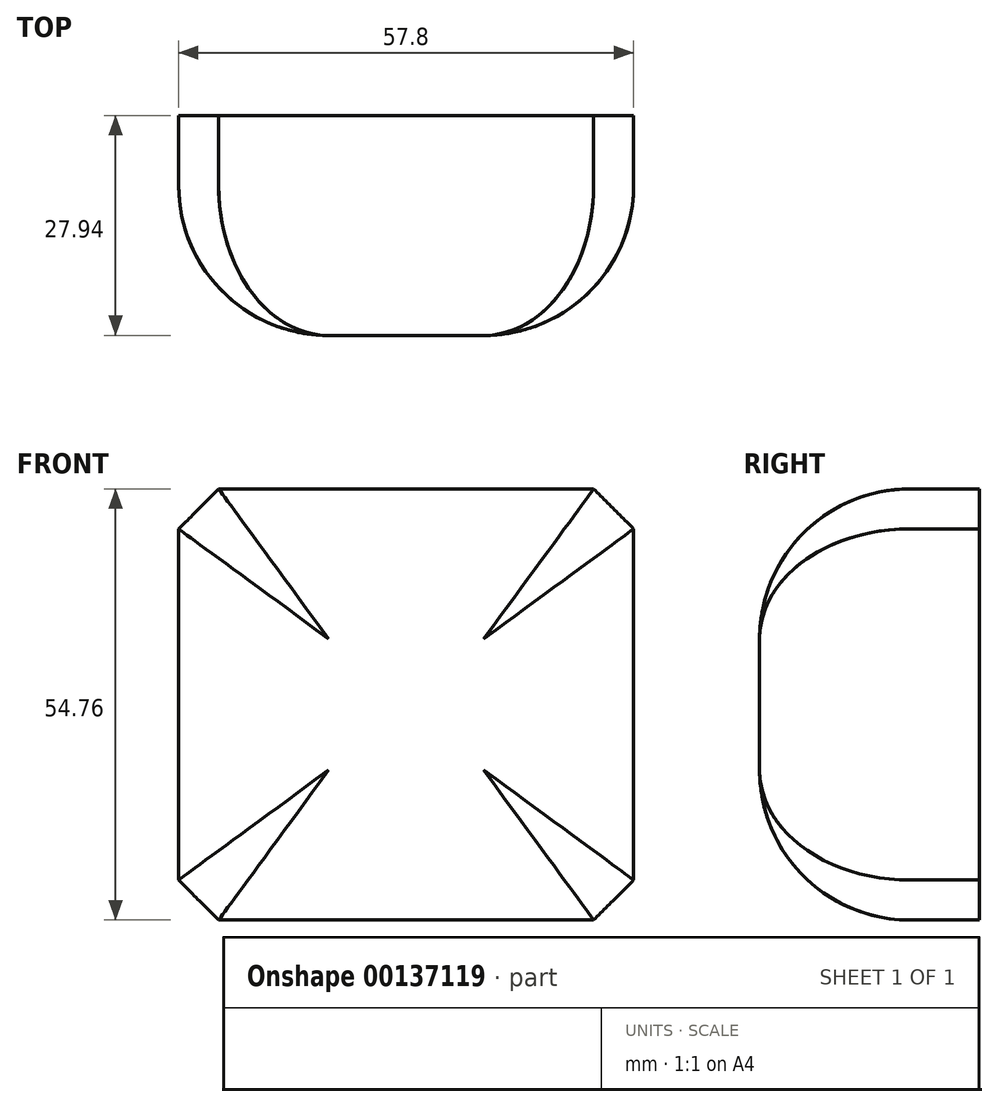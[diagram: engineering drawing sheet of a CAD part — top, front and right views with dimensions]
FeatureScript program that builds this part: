
annotation { "Feature Type Name" : "Feature", "Feature Type Description" : "" }
export const myFeature = defineFeature(function(context is Context, id is Id, definition is map)
    precondition{}
    {
        {
            var Q0;
            Q0=qCreatedBy(makeId("Front.planeOp"),FACE);
            var sketch = newSketch(context, id + "F0", { "sketchPlane" : qUnion([Q0])});
            skLineSegment(sketch, "E0.bottom", {"start": v(-40.16, 61.96) * mm, "end": v(17.64, 61.96) * mm});
            skLineSegment(sketch, "E0.top", {"start": v(-40.16, 7.2) * mm, "end": v(17.64, 7.2) * mm});
            skLineSegment(sketch, "E0.left", {"start": v(-40.16, 61.96) * mm, "end": v(-40.16, 7.2) * mm});
            skLineSegment(sketch, "E0.right", {"start": v(17.64, 61.96) * mm, "end": v(17.64, 7.2) * mm});
            skSolve(sketch);
        }
        {
            var Q0;
            Q0=makeQuery(id+"F0.imprint","IMPRINT",FACE,{"disambiguationData":[TD([[makeQuery(id+"F0.imprint","IMPRINT",EDGE,{"derivedFrom":sQuery(id+"F0.wireOp",EDGE,"E0.bottom")}),-1.0]])]});
            extrude(context, id + "F1", {"entities" : qUnion([Q0]), "depth" : 27.94 * mm});
        }
        {
            var Q0;
            Q0=makeQuery(id+"F1.opExtrude","CAP_EDGE",EDGE,{"disambiguationData":[OSD([sQuery(id+"F0.wireOp",EDGE,"E0.bottom")])],"isStart":false});
            var Q1;
            Q1=makeQuery(id+"F1.opExtrude","CAP_EDGE",EDGE,{"disambiguationData":[OSD([sQuery(id+"F0.wireOp",EDGE,"E0.right")])],"isStart":false});
            var Q2;
            Q2=makeQuery(id+"F1.opExtrude","CAP_EDGE",EDGE,{"disambiguationData":[OSD([sQuery(id+"F0.wireOp",EDGE,"E0.top")])],"isStart":false});
            var Q3;
            Q3=makeQuery(id+"F1.opExtrude","CAP_EDGE",EDGE,{"disambiguationData":[OSD([sQuery(id+"F0.wireOp",EDGE,"E0.left")])],"isStart":false});
            fillet(context, id + "F2", {"entities" : qUnion([Q0, Q1, Q2, Q3]), "radius" : 19.05 * mm, "tangentPropagation" : true, "allowEdgeOverflow" : false});
        }
        {
            var Q0;
            Q0=makeQuery(id+"F1.opExtrude","SWEPT_EDGE",EDGE,{"disambiguationData":[OSD([sQuery(id+"F0.wireOp",EDGE,"E0.bottom"),sQuery(id+"F0.wireOp",EDGE,"E0.right")])]});
            var Q1;
            Q1=makeQuery(id+"F1.opExtrude","SWEPT_EDGE",EDGE,{"disambiguationData":[OSD([sQuery(id+"F0.wireOp",EDGE,"E0.top"),sQuery(id+"F0.wireOp",EDGE,"E0.right")])]});
            var Q2;
            Q2=makeQuery(id+"F1.opExtrude","SWEPT_EDGE",EDGE,{"disambiguationData":[OSD([sQuery(id+"F0.wireOp",EDGE,"E0.bottom"),sQuery(id+"F0.wireOp",EDGE,"E0.left")])]});
            var Q3;
            Q3=makeQuery(id+"F1.opExtrude","SWEPT_EDGE",EDGE,{"disambiguationData":[OSD([sQuery(id+"F0.wireOp",EDGE,"E0.top"),sQuery(id+"F0.wireOp",EDGE,"E0.left")])]});
            chamfer(context, id + "F3", {"entities" : qUnion([Q0, Q1, Q2, Q3]), "width" : 5.08 * mm, "tangentPropagation" : true});
        }
    });
